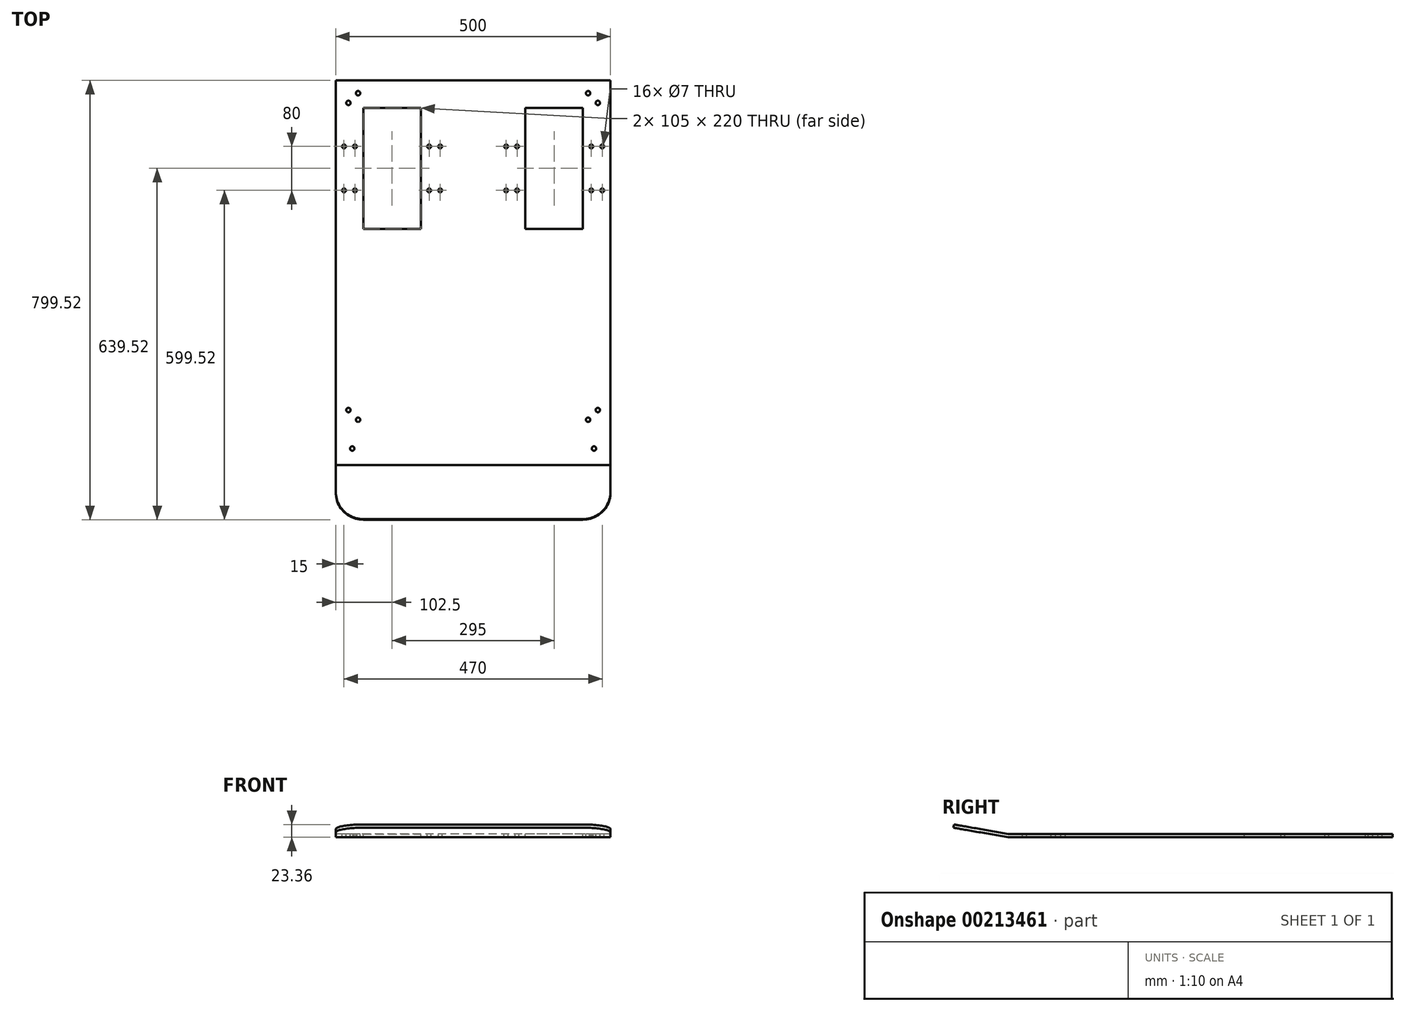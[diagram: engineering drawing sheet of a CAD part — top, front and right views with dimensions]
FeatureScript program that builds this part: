
annotation { "Feature Type Name" : "Feature", "Feature Type Description" : "" }
export const myFeature = defineFeature(function(context is Context, id is Id, definition is map)
    precondition{}
    {
        {
            var Q0;
            Q0=qCreatedBy(makeId("Right.planeOp"),FACE);
            var sketch = newSketch(context, id + "F0", { "sketchPlane" : qUnion([Q0])});
            skLineSegment(sketch, "E0.bottom", {"start": v(0, 0) * mm, "end": v(700, 0) * mm});
            skLineSegment(sketch, "E0.top", {"start": v(0, -6) * mm, "end": v(700, -6) * mm});
            skLineSegment(sketch, "E0.right", {"start": v(700, 0) * mm, "end": v(700, -6) * mm});
            skLineSegment(sketch, "E1", {"start": v(0, 0) * mm, "end": v(-98.48, 17.36) * mm});
            skLineSegment(sketch, "E2", {"start": v(-98.48, 17.36) * mm, "end": v(-99.52, 11.46) * mm});
            skLineSegment(sketch, "E3", {"start": v(-99.52, 11.46) * mm, "end": v(0, -6) * mm});
            skSolve(sketch);
        }
        {
            var Q0;
            Q0=makeQuery(id+"F0.imprint","IMPRINT",FACE,{"disambiguationData":[TD([[makeQuery(id+"F0.imprint","IMPRINT",EDGE,{"derivedFrom":sQuery(id+"F0.wireOp",EDGE,"E0.bottom")}),-1.0]])]});
            extrude(context, id + "F1", {"entities" : qUnion([Q0]), "depth" : 500 * mm});
        }
        {
            var Q0;
            Q0=makeQuery(id+"F1.opExtrude","SWEPT_FACE",FACE,{"disambiguationData":[OSD([sQuery(id+"F0.wireOp",EDGE,"E1")])]});
            var sketch = newSketch(context, id + "F2", { "sketchPlane" : qUnion([Q0])});
            skLineSegment(sketch, "E4", {"start": v(50, -100) * mm, "end": v(450, -100) * mm});
            skPoint(sketch, "E5.visualSharp", {"position": v(0, -100) * mm});
            skArc(sketch, "E5.filletArc", {"start": v(0, -50) * mm, "mid": v(14.64, -85.36) * mm, "end": v(50, -100) * mm});
            skPoint(sketch, "E6.visualSharp", {"position": v(500, -100) * mm});
            skArc(sketch, "E6.filletArc", {"start": v(450, -100) * mm, "mid": v(485.36, -85.36) * mm, "end": v(500, -50) * mm});
            skLineSegment(sketch, "E7.left", {"start": v(0, -50) * mm, "end": v(0, -50) * mm});
            skLineSegment(sketch, "E8", {"start": v(0, -50) * mm, "end": v(-35.02, -50) * mm});
            skLineSegment(sketch, "E9", {"start": v(-35.02, -50) * mm, "end": v(-35.02, -125.84) * mm});
            skLineSegment(sketch, "E10", {"start": v(-35.02, -125.84) * mm, "end": v(549.5, -125.84) * mm});
            skLineSegment(sketch, "E11", {"start": v(549.5, -125.84) * mm, "end": v(549.5, -50) * mm});
            skLineSegment(sketch, "E12", {"start": v(549.5, -50) * mm, "end": v(500, -50) * mm});
            skSolve(sketch);
        }
        {
            var Q0;
            {var subQ0=sQuery(id+"F2.wireOp",EDGE,"E5.filletArc");Q0=makeQuery(id+"F2.imprint","IMPRINT",FACE,{"disambiguationData":[TD([[makeQuery(id+"F2.imprint","IMPRINT",EDGE,{"derivedFrom":subQ0}),-1.0]])]});}
            var Q1;
            {var subQ0=sQuery(id+"F2.wireOp",EDGE,"E6.filletArc");Q1=makeQuery(id+"F2.imprint","IMPRINT",FACE,{"disambiguationData":[TD([[makeQuery(id+"F2.imprint","IMPRINT",EDGE,{"derivedFrom":subQ0}),-1.0]])]});}
            extrude(context, id + "F3", {"entities" : qUnion([Q0, Q1]), "operationType" : NewBodyOperationType.REMOVE, "endBound" : BoundingType.THROUGH_ALL, "oppositeDirection" : true, "depth" : 25 * mm});
        }
        {
            var Q0;
            Q0=makeQuery(id+"F1.opExtrude","SWEPT_FACE",FACE,{"disambiguationData":[OSD([sQuery(id+"F0.wireOp",EDGE,"E0.bottom")])]});
            var sketch = newSketch(context, id + "F4", { "sketchPlane" : qUnion([Q0])});
            skLineSegment(sketch, "E13.bottom", {"start": v(50, 430) * mm, "end": v(155, 430) * mm});
            skLineSegment(sketch, "E13.top", {"start": v(50, 650) * mm, "end": v(155, 650) * mm});
            skLineSegment(sketch, "E13.left", {"start": v(50, 430) * mm, "end": v(50, 650) * mm});
            skLineSegment(sketch, "E13.right", {"start": v(155, 430) * mm, "end": v(155, 650) * mm});
            skLineSegment(sketch, "E14", {"start": v(250, 0) * mm, "end": v(250, 700) * mm, "construction": true});
            skLineSegment(sketch, "E15", {"start": v(50, 540) * mm, "end": v(155, 540) * mm, "construction": true});
            skLineSegment(sketch, "E16", {"start": v(102.5, 430) * mm, "end": v(102.5, 650) * mm, "construction": true});
            skCircle(sketch, "E17", {"center": v(35, 500) * mm, "radius": 3.5 * mm});
            skCircle(sketch, "E18", {"center": v(15, 500) * mm, "radius": 3.5 * mm});
            skCircle(sketch, "E19.MirrorC", {"center": v(35, 580) * mm, "radius": 3.5 * mm});
            skCircle(sketch, "E20.MirrorC", {"center": v(15, 580) * mm, "radius": 3.5 * mm});
            skCircle(sketch, "E21.MirrorC", {"center": v(190, 500) * mm, "radius": 3.5 * mm});
            skCircle(sketch, "E22.MirrorC", {"center": v(170, 500) * mm, "radius": 3.5 * mm});
            skCircle(sketch, "E23.MirrorC", {"center": v(190, 580) * mm, "radius": 3.5 * mm});
            skCircle(sketch, "E24.MirrorC", {"center": v(170, 580) * mm, "radius": 3.5 * mm});
            skCircle(sketch, "E25.MirrorC", {"center": v(465, 500) * mm, "radius": 3.5 * mm});
            skCircle(sketch, "E26.MirrorC", {"center": v(485, 500) * mm, "radius": 3.5 * mm});
            skCircle(sketch, "E27.MirrorC", {"center": v(485, 580) * mm, "radius": 3.5 * mm});
            skCircle(sketch, "E28.MirrorC", {"center": v(310, 500) * mm, "radius": 3.5 * mm});
            skCircle(sketch, "E29.MirrorC", {"center": v(465, 580) * mm, "radius": 3.5 * mm});
            skCircle(sketch, "E30.MirrorC", {"center": v(330, 500) * mm, "radius": 3.5 * mm});
            skCircle(sketch, "E31.MirrorC", {"center": v(330, 580) * mm, "radius": 3.5 * mm});
            skCircle(sketch, "E32.MirrorC", {"center": v(310, 580) * mm, "radius": 3.5 * mm});
            skLineSegment(sketch, "E33.MirrorCS", {"start": v(397.5, 430) * mm, "end": v(397.5, 650) * mm, "construction": true});
            skLineSegment(sketch, "E34.MirrorCS", {"start": v(450, 540) * mm, "end": v(345, 540) * mm, "construction": true});
            skLineSegment(sketch, "E35.MirrorCS", {"start": v(345, 430) * mm, "end": v(345, 650) * mm});
            skLineSegment(sketch, "E36.MirrorCS", {"start": v(450, 430) * mm, "end": v(450, 650) * mm});
            skLineSegment(sketch, "E37.MirrorCS", {"start": v(450, 650) * mm, "end": v(345, 650) * mm});
            skLineSegment(sketch, "E38.MirrorCS", {"start": v(450, 430) * mm, "end": v(345, 430) * mm});
            skLineSegment(sketch, "E39", {"start": v(-100.8, 30) * mm, "end": v(560.47, 30) * mm, "construction": true});
            skLineSegment(sketch, "E40", {"start": v(30, 88.03) * mm, "end": v(30, 30) * mm, "construction": true});
            skCircle(sketch, "E41", {"center": v(30, 30) * mm, "radius": 4 * mm});
            skCircle(sketch, "E42.MirrorC", {"center": v(470, 30) * mm, "radius": 4 * mm});
            skSolve(sketch);
        }
        {
            var Q0;
            Q0 = qSketchRegion(id + "F4", true);
            extrude(context, id + "F5", {"entities" : qUnion([Q0]), "operationType" : NewBodyOperationType.REMOVE, "endBound" : BoundingType.THROUGH_ALL, "oppositeDirection" : true, "depth" : 25 * mm});
        }
        {
            var Q0;
            Q0=makeQuery(id+"F1.opExtrude","SWEPT_FACE",FACE,{"disambiguationData":[OSD([sQuery(id+"F0.wireOp",EDGE,"E0.bottom")])]});
            var sketch = newSketch(context, id + "F6", { "sketchPlane" : qUnion([Q0])});
            skCircle(sketch, "E43", {"center": v(23, 100) * mm, "radius": 4 * mm});
            skLineSegment(sketch, "E44", {"start": v(23, 100) * mm, "end": v(40.68, 82.32) * mm, "construction": true});
            skCircle(sketch, "E45", {"center": v(40.68, 82.32) * mm, "radius": 4 * mm});
            skLineSegment(sketch, "E46", {"start": v(250, 700) * mm, "end": v(250, 0) * mm, "construction": true});
            skCircle(sketch, "E47", {"center": v(23, 659.32) * mm, "radius": 4 * mm});
            skLineSegment(sketch, "E48", {"start": v(23, 659.32) * mm, "end": v(40.68, 677) * mm, "construction": true});
            skCircle(sketch, "E49", {"center": v(40.68, 677) * mm, "radius": 4 * mm});
            skCircle(sketch, "E50.MirrorC", {"center": v(459.32, 677) * mm, "radius": 4 * mm});
            skCircle(sketch, "E51.MirrorC", {"center": v(477, 659.32) * mm, "radius": 4 * mm});
            skCircle(sketch, "E52.MirrorC", {"center": v(477, 100) * mm, "radius": 4 * mm});
            skCircle(sketch, "E53.MirrorC", {"center": v(459.32, 82.32) * mm, "radius": 4 * mm});
            skSolve(sketch);
        }
        {
            var Q0;
            Q0 = qSketchRegion(id + "F6", true);
            extrude(context, id + "F7", {"entities" : qUnion([Q0]), "operationType" : NewBodyOperationType.REMOVE, "endBound" : BoundingType.THROUGH_ALL, "oppositeDirection" : true, "depth" : 25 * mm});
        }
    });
